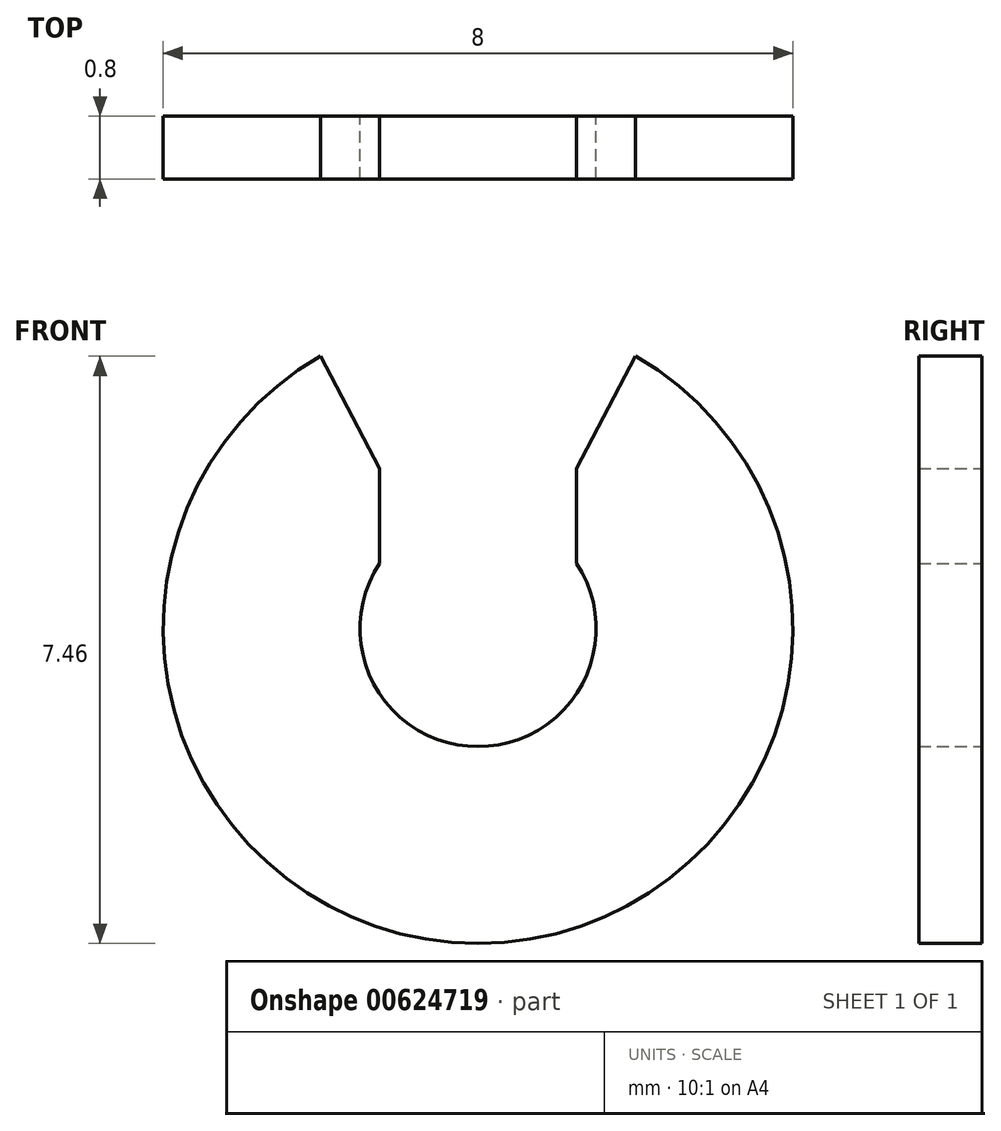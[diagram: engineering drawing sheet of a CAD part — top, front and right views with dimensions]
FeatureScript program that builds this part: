
annotation { "Feature Type Name" : "Feature", "Feature Type Description" : "" }
export const myFeature = defineFeature(function(context is Context, id is Id, definition is map)
    precondition{}
    {
        {
            var Q0;
            Q0=qCreatedBy(makeId("Front.planeOp"),FACE);
            var sketch = newSketch(context, id + "F0", { "sketchPlane" : qUnion([Q0])});
            skArc(sketch, "E0", {"start": v(-2, 3.46) * mm, "mid": v(0, -4) * mm, "end": v(2, 3.46) * mm});
            skArc(sketch, "E1", {"start": v(-1.25, 0.83) * mm, "mid": v(0, -1.5) * mm, "end": v(1.25, 0.83) * mm});
            skLineSegment(sketch, "E2", {"start": v(-1.25, 0.83) * mm, "end": v(-1.25, 2.03) * mm});
            skLineSegment(sketch, "E3", {"start": v(1.25, 0.83) * mm, "end": v(1.25, 2.03) * mm});
            skLineSegment(sketch, "E4", {"start": v(-1.25, 2.03) * mm, "end": v(-2, 3.46) * mm});
            skLineSegment(sketch, "E5", {"start": v(2, 3.46) * mm, "end": v(1.25, 2.03) * mm});
            skSolve(sketch);
        }
        {
            var Q0;
            Q0=makeQuery(id+"F0.imprint","IMPRINT",FACE,{"disambiguationData":[TD([[makeQuery(id+"F0.imprint","IMPRINT",EDGE,{"derivedFrom":sQuery(id+"F0.wireOp",EDGE,"E0")}),1.0]])]});
            extrude(context, id + "F1", {"entities" : qUnion([Q0]), "depth" : 0.8 * mm, "offsetDistance" : 25 * mm});
        }
    });
